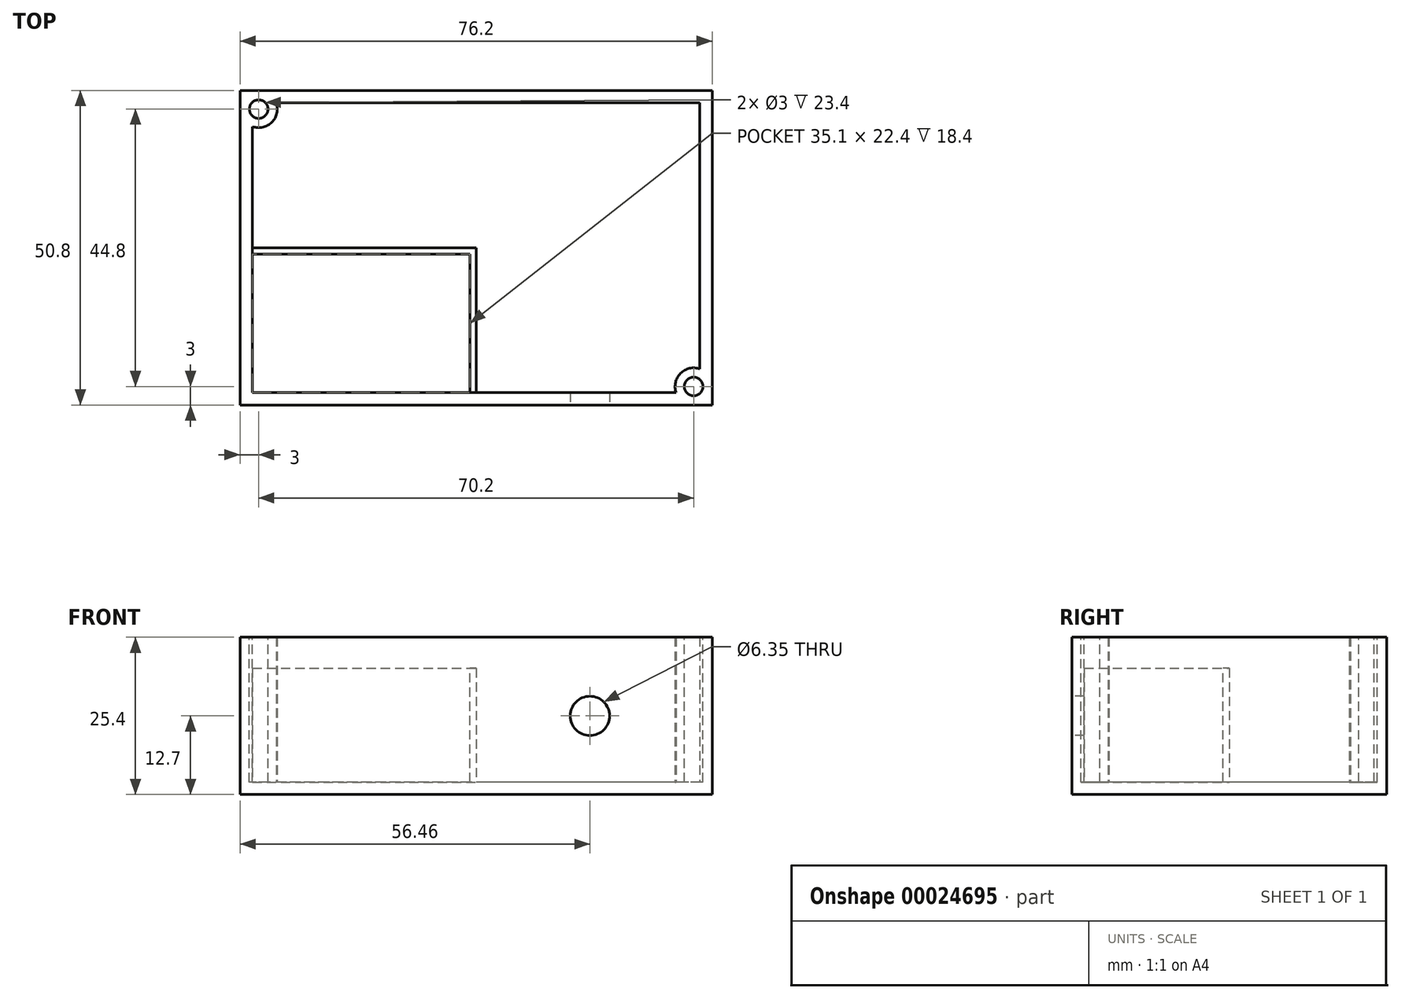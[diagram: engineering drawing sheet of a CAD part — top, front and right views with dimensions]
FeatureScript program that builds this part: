
annotation { "Feature Type Name" : "Feature", "Feature Type Description" : "" }
export const myFeature = defineFeature(function(context is Context, id is Id, definition is map)
    precondition{}
    {
        {
            var Q0;
            Q0=qCreatedBy(makeId("Top.planeOp"),FACE);
            var sketch = newSketch(context, id + "F0", { "sketchPlane" : qUnion([Q0])});
            skLineSegment(sketch, "E0.rect.bottom", {"start": v(38.1, 25.4) * mm, "end": v(-38.1, 25.4) * mm});
            skLineSegment(sketch, "E0.rect.top", {"start": v(38.1, -25.4) * mm, "end": v(-38.1, -25.4) * mm});
            skLineSegment(sketch, "E0.rect.left", {"start": v(38.1, 25.4) * mm, "end": v(38.1, -25.4) * mm});
            skLineSegment(sketch, "E0.rect.right", {"start": v(-38.1, 25.4) * mm, "end": v(-38.1, -25.4) * mm});
            skPoint(sketch, "E0.rect.middle", {"position": v(0, 0) * mm});
            skSolve(sketch);
        }
        {
            var Q0;
            Q0 = qSketchRegion(id + "F0", true);
            extrude(context, id + "F1", {"entities" : qUnion([Q0]), "depth" : 25.4 * mm});
        }
        {
            var Q0;
            Q0=makeQuery(id+"F1.opExtrude","CAP_FACE",FACE,{"disambiguationData":[OSD([sQuery(id+"F0.wireOp",EDGE,"E0.rect.bottom"),sQuery(id+"F0.wireOp",EDGE,"E0.rect.top"),sQuery(id+"F0.wireOp",EDGE,"E0.rect.left"),sQuery(id+"F0.wireOp",EDGE,"E0.rect.right")])],"isStart":false});
            var sketch = newSketch(context, id + "F2", { "sketchPlane" : qUnion([Q0])});
            skLineSegment(sketch, "E1.rect.bottom", {"start": v(36.1, 23.4) * mm, "end": v(-36.1, 23.4) * mm});
            skLineSegment(sketch, "E1.rect.top", {"start": v(36.1, -23.4) * mm, "end": v(-36.1, -23.4) * mm});
            skLineSegment(sketch, "E1.rect.left", {"start": v(36.1, 23.4) * mm, "end": v(36.1, -23.4) * mm});
            skLineSegment(sketch, "E1.rect.right", {"start": v(-36.1, 23.4) * mm, "end": v(-36.1, -23.4) * mm});
            skPoint(sketch, "E1.rect.middle", {"position": v(0, 0) * mm});
            skSolve(sketch);
        }
        {
            var Q0;
            Q0 = qSketchRegion(id + "F2", true);
            extrude(context, id + "F3", {"entities" : qUnion([Q0]), "operationType" : NewBodyOperationType.REMOVE, "oppositeDirection" : true, "depth" : 25.4 * mm - 2 * mm});
        }
        {
            var Q0;
            Q0=makeQuery(id+"F3.boolean.opBoolean","COPY",FACE,{"derivedFrom":makeQuery(id+"F3.opExtrude","CAP_FACE",FACE,{"disambiguationData":[OSD([sQuery(id+"F2.wireOp",EDGE,"E1.rect.bottom"),sQuery(id+"F2.wireOp",EDGE,"E1.rect.top"),sQuery(id+"F2.wireOp",EDGE,"E1.rect.left"),sQuery(id+"F2.wireOp",EDGE,"E1.rect.right")])],"isStart":false})});
            var sketch = newSketch(context, id + "F4", { "sketchPlane" : qUnion([Q0])});
            skCircle(sketch, "E2", {"center": v(-35.1, 22.4) * mm, "radius": 3 * mm});
            skCircle(sketch, "E3", {"center": v(35.1, -22.4) * mm, "radius": 3 * mm});
            skSolve(sketch);
        }
        {
            var Q0;
            Q0 = qSketchRegion(id + "F4", true);
            extrude(context, id + "F5", {"entities" : qUnion([Q0]), "operationType" : NewBodyOperationType.ADD, "depth" : 25.4 * mm - 2 * mm});
        }
        {
            var Q0;
            Q0=makeQuery(id+"F5.boolean.opBoolean","MERGE",FACE,{"derivedFrom":[makeQuery(id+"F1.opExtrude","CAP_FACE",FACE,{"disambiguationData":[OSD([sQuery(id+"F0.wireOp",EDGE,"E0.rect.bottom"),sQuery(id+"F0.wireOp",EDGE,"E0.rect.top"),sQuery(id+"F0.wireOp",EDGE,"E0.rect.left"),sQuery(id+"F0.wireOp",EDGE,"E0.rect.right")])],"isStart":false}),makeQuery(id+"F5.opExtrude","CAP_FACE",FACE,{"disambiguationData":[OSD([sQuery(id+"F4.wireOp",EDGE,"E2")])],"isStart":false}),makeQuery(id+"F5.opExtrude","CAP_FACE",FACE,{"disambiguationData":[OSD([sQuery(id+"F4.wireOp",EDGE,"E3")])],"isStart":false})]});
            var sketch = newSketch(context, id + "F6", { "sketchPlane" : qUnion([Q0])});
            skCircle(sketch, "E4", {"center": v(-35.1, 22.4) * mm, "radius": 1.5 * mm});
            skCircle(sketch, "E5", {"center": v(35.1, -22.4) * mm, "radius": 1.5 * mm});
            skSolve(sketch);
        }
        {
            var Q0;
            Q0 = qSketchRegion(id + "F6", true);
            extrude(context, id + "F7", {"entities" : qUnion([Q0]), "operationType" : NewBodyOperationType.REMOVE, "oppositeDirection" : true, "depth" : 25.4 * mm - 2 * mm});
        }
        {
            var Q0;
            Q0=makeQuery(id+"F3.boolean.opBoolean","COPY",FACE,{"derivedFrom":makeQuery(id+"F3.opExtrude","CAP_FACE",FACE,{"disambiguationData":[OSD([sQuery(id+"F2.wireOp",EDGE,"E1.rect.bottom"),sQuery(id+"F2.wireOp",EDGE,"E1.rect.top"),sQuery(id+"F2.wireOp",EDGE,"E1.rect.left"),sQuery(id+"F2.wireOp",EDGE,"E1.rect.right")])],"isStart":false})});
            var sketch = newSketch(context, id + "F8", { "sketchPlane" : qUnion([Q0])});
            skLineSegment(sketch, "E6.bottom", {"start": v(-36.1, -23.4) * mm, "end": v(0, -23.4) * mm});
            skLineSegment(sketch, "E6.top", {"start": v(-36.1, 0) * mm, "end": v(0, 0) * mm});
            skLineSegment(sketch, "E6.left", {"start": v(-36.1, -23.4) * mm, "end": v(-36.1, 0) * mm});
            skLineSegment(sketch, "E6.right", {"start": v(0, -23.4) * mm, "end": v(0, 0) * mm});
            skSolve(sketch);
        }
        {
            var Q0;
            Q0 = qSketchRegion(id + "F8", true);
            extrude(context, id + "F9", {"entities" : qUnion([Q0]), "operationType" : NewBodyOperationType.ADD, "depth" : 25.4 * mm - 2 * mm});
        }
        {
            var Q0;
            Q0=makeQuery(id+"F9.boolean.opBoolean","MERGE",FACE,{"derivedFrom":[makeQuery(id+"F5.boolean.opBoolean","MERGE",FACE,{"derivedFrom":[makeQuery(id+"F1.opExtrude","CAP_FACE",FACE,{"disambiguationData":[OSD([sQuery(id+"F0.wireOp",EDGE,"E0.rect.bottom"),sQuery(id+"F0.wireOp",EDGE,"E0.rect.top"),sQuery(id+"F0.wireOp",EDGE,"E0.rect.left"),sQuery(id+"F0.wireOp",EDGE,"E0.rect.right")])],"isStart":false}),makeQuery(id+"F5.opExtrude","CAP_FACE",FACE,{"disambiguationData":[OSD([sQuery(id+"F4.wireOp",EDGE,"E2")])],"isStart":false}),makeQuery(id+"F5.opExtrude","CAP_FACE",FACE,{"disambiguationData":[OSD([sQuery(id+"F4.wireOp",EDGE,"E3")])],"isStart":false})]}),makeQuery(id+"F9.opExtrude","CAP_FACE",FACE,{"disambiguationData":[OSD([sQuery(id+"F8.wireOp",EDGE,"E6.bottom"),sQuery(id+"F8.wireOp",EDGE,"E6.top"),sQuery(id+"F8.wireOp",EDGE,"E6.left"),sQuery(id+"F8.wireOp",EDGE,"E6.right")])],"isStart":false})]});
            var sketch = newSketch(context, id + "F10", { "sketchPlane" : qUnion([Q0])});
            skLineSegment(sketch, "E7.bottom", {"start": v(-1, -1) * mm, "end": v(-36.1, -1) * mm});
            skLineSegment(sketch, "E7.top", {"start": v(-1, -23.4) * mm, "end": v(-36.1, -23.4) * mm});
            skLineSegment(sketch, "E7.left", {"start": v(-1, -1) * mm, "end": v(-1, -23.4) * mm});
            skLineSegment(sketch, "E7.right", {"start": v(-36.1, -1) * mm, "end": v(-36.1, -23.4) * mm});
            skSolve(sketch);
        }
        {
            var Q0;
            Q0 = qSketchRegion(id + "F10", true);
            extrude(context, id + "F11", {"entities" : qUnion([Q0]), "operationType" : NewBodyOperationType.REMOVE, "oppositeDirection" : true, "depth" : 25.4 * mm - 2 * mm});
        }
        {
            var Q0;
            Q0=makeQuery(id+"F9.boolean.opBoolean","MERGE",FACE,{"derivedFrom":[makeQuery(id+"F5.boolean.opBoolean","MERGE",FACE,{"derivedFrom":[makeQuery(id+"F1.opExtrude","CAP_FACE",FACE,{"disambiguationData":[OSD([sQuery(id+"F0.wireOp",EDGE,"E0.rect.bottom"),sQuery(id+"F0.wireOp",EDGE,"E0.rect.top"),sQuery(id+"F0.wireOp",EDGE,"E0.rect.left"),sQuery(id+"F0.wireOp",EDGE,"E0.rect.right")])],"isStart":false}),makeQuery(id+"F5.opExtrude","CAP_FACE",FACE,{"disambiguationData":[OSD([sQuery(id+"F4.wireOp",EDGE,"E2")])],"isStart":false}),makeQuery(id+"F5.opExtrude","CAP_FACE",FACE,{"disambiguationData":[OSD([sQuery(id+"F4.wireOp",EDGE,"E3")])],"isStart":false})]}),makeQuery(id+"F9.opExtrude","CAP_FACE",FACE,{"disambiguationData":[OSD([sQuery(id+"F8.wireOp",EDGE,"E6.bottom"),sQuery(id+"F8.wireOp",EDGE,"E6.top"),sQuery(id+"F8.wireOp",EDGE,"E6.left"),sQuery(id+"F8.wireOp",EDGE,"E6.right")])],"isStart":false})]});
            var sketch = newSketch(context, id + "F12", { "sketchPlane" : qUnion([Q0])});
            skLineSegment(sketch, "E8.bottom", {"start": v(-36.1, -23.4) * mm, "end": v(8.4, -23.4) * mm});
            skLineSegment(sketch, "E8.top", {"start": v(-36.1, 5.7) * mm, "end": v(8.4, 5.7) * mm});
            skLineSegment(sketch, "E8.left", {"start": v(-36.1, -23.4) * mm, "end": v(-36.1, 5.7) * mm});
            skLineSegment(sketch, "E8.right", {"start": v(8.4, -23.4) * mm, "end": v(8.4, 5.7) * mm});
            skSolve(sketch);
        }
        {
            var Q0;
            Q0 = qSketchRegion(id + "F12", true);
            extrude(context, id + "F13", {"entities" : qUnion([Q0]), "operationType" : NewBodyOperationType.REMOVE, "oppositeDirection" : true, "depth" : 5 * mm});
        }
        {
            var Q0;
            Q0=makeQuery(id+"F1.opExtrude","SWEPT_FACE",FACE,{"disambiguationData":[OSD([sQuery(id+"F0.wireOp",EDGE,"E0.rect.top")])]});
            var sketch = newSketch(context, id + "F14", { "sketchPlane" : qUnion([Q0])});
            skCircle(sketch, "E9", {"center": v(18.36, 12.7) * mm, "radius": 3.18 * mm});
            skSolve(sketch);
        }
        {
            var Q0;
            Q0=makeQuery(id+"F14.imprint","IMPRINT",FACE,{"disambiguationData":[TD([[makeQuery(id+"F14.imprint","IMPRINT",EDGE,{"derivedFrom":sQuery(id+"F14.wireOp",EDGE,"E9")}),1.0]])]});
            extrude(context, id + "F15", {"entities" : qUnion([Q0]), "operationType" : NewBodyOperationType.REMOVE, "oppositeDirection" : true, "depth" : 2 * mm});
        }
    });
